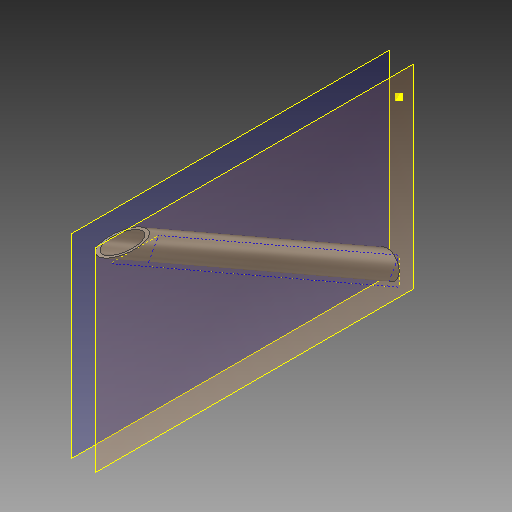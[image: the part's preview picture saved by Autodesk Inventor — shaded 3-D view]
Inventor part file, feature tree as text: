
AUTODESK INVENTOR PART (.ipt)
format: ipt  version: 2018 (Build 220112000, 112)  size: 131,584 bytes
history: native  units: mm
features: other x4, sketch x3, extrude x2, projected_geometry x1
ambient origin geometry x8: Origin, YZ Plane, XZ Plane, XY Plane, X Axis, Y Axis, Z Axis, Center Point
bodies: Body1 (feature_tree)
feature tree (10):
  other  "ソリッド1"
  sketch  "スケッチ1"
  other  "作業平面1"
  extrude  "押し出し1"  Depth=186.4mm
  extrude  "押し出し2"  Depth=326.4mm
  other  "作業平面2"
  other  "作業平面3"
  sketch  "スケッチ4"
  sketch  "スケッチ3"
  projected_geometry  "投影ループ1"
